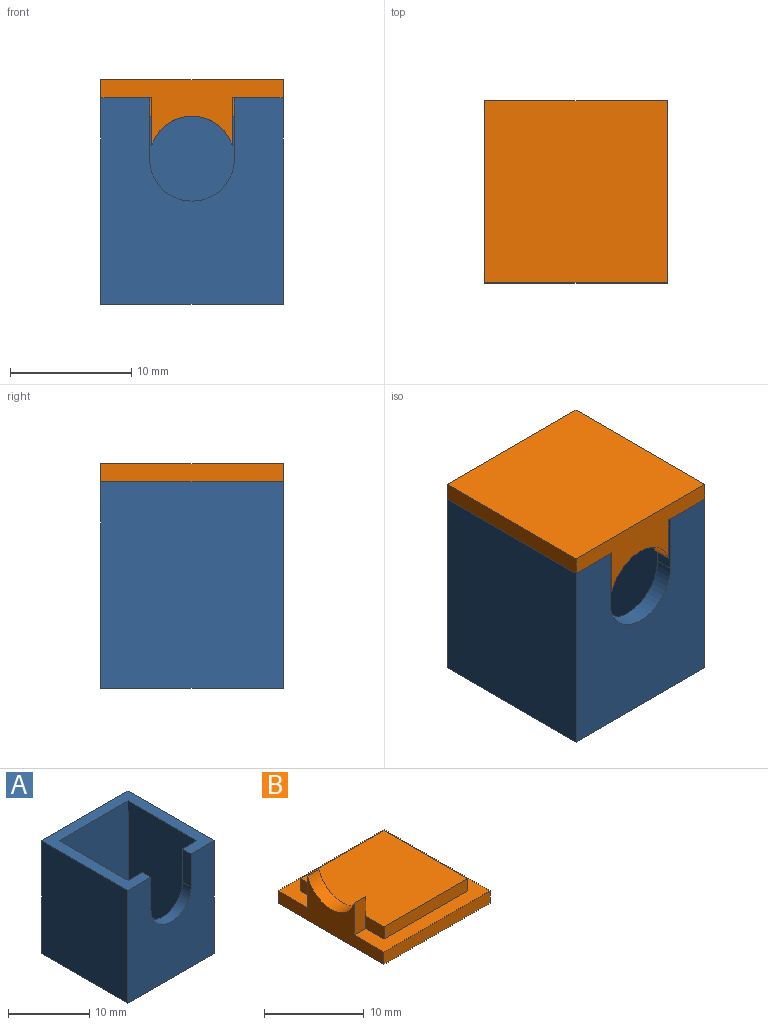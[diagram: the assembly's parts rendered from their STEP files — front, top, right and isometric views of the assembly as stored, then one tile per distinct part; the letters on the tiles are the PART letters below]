
ASSEMBLY  parts=2 mates=1
PART A: 18 faces, bbox 15x15x17 mm
  f0: plane 17x15mm, normal (0,-1,0), area 200.8mm2, adj f1,f3,f8,f9,f15,f16,f17
  f1: plane 15x15mm, normal (0,0,1), area 70.5mm2, adj f0,f2,f3,f4,f5,f6,f7,f8
  f2: plane 17x15mm, normal (0,1,0), area 255mm2, adj f1,f3,f8,f9
  f3: plane 17x15mm, normal (-1,0,0), area 255mm2, adj f0,f1,f2,f9
  f4: plane 15.5x12mm, normal (1,0,0), area 186mm2, adj f1,f5,f7,f14
  f5: plane 15.5x12mm, normal (0,-1,0), area 186mm2, adj f1,f4,f6,f14
  f6: plane 15.5x12mm, normal (-1,0,0), area 186mm2, adj f1,f5,f7,f14
  f7: plane 15.5x12mm, normal (0,1,0), area 131.8mm2, adj f1,f4,f6,f14,f15,f16,f17
  f8: plane 17x15mm, normal (1,0,0), area 255mm2, adj f0,f1,f2,f9
  f9: plane 15x15mm, normal (0,0,-1), area 219mm2, adj f0,f2,f3,f8,f10,f11,f12,f13
  f10: plane 2x1.5mm, normal (-1,0,0), area 3mm2, adj f9,f11,f13,f14
  f11: plane 3x1.5mm, normal (0,1,0), area 4.5mm2, adj f9,f10,f12,f14
  f12: plane 2x1.5mm, normal (1,0,0), area 3mm2, adj f9,f11,f13,f14
  f13: plane 3x1.5mm, normal (0,-1,0), area 4.5mm2, adj f9,f10,f12,f14
  f14: plane 12x12mm, normal (0,0,1), area 138mm2, adj f4,f5,f6,f7,f10,f11,f12,f13
  f15: cylinder r=3.5mm len=7mm, axis (0,-1,0), area 16.5mm2, adj f0,f7,f16,f17
  f16: plane 5x1.5mm, normal (-1,0,0), area 7.5mm2, adj f0,f1,f7,f15
  f17: plane 5x1.5mm, normal (1,0,0), area 7.5mm2, adj f0,f1,f7,f15
PART B: 17 faces, bbox 15x15x5.4 mm
  f0: plane 3.91x1.63mm, normal (0,1,0), area 6.3mm2, adj f2,f4,f14,f15,f16
  f1: plane 3.91x1.63mm, normal (0,-1,0), area 6.3mm2, adj f2,f3,f5,f14,f16
  f2: plane 15x5.41mm, normal (-1,0,0), area 36.8mm2, adj f0,f1,f10,f11,f13,f14,f16
  f3: plane 3.33x2.41mm, normal (1,0,0), area 2.1mm2, adj f1,f9,f16
  f4: plane 2.55x1.5mm, normal (-1,0,0), area 3.8mm2, adj f0,f8,f9,f14
  f5: plane 2.55x1.5mm, normal (-1,0,0), area 3.8mm2, adj f1,f6,f9,f14
  f6: plane 11.75x1.5mm, normal (0,-1,0), area 17.6mm2, adj f5,f7,f9,f14
  f7: plane 11.75x1.5mm, normal (1,0,0), area 17.6mm2, adj f6,f8,f9,f14
  f8: plane 11.75x1.5mm, normal (0,1,0), area 17.6mm2, adj f4,f7,f9,f14
  f9: plane 11.75x11.75mm, normal (0,0,1), area 138.1mm2, adj f3,f4,f5,f6,f7,f8,f15
  f10: plane 15x15mm, normal (0,0,-1), area 225mm2, adj f2,f11,f12,f13
  f11: plane 15x1.5mm, normal (0,-1,0), area 22.5mm2, adj f2,f10,f12,f14
  f12: plane 15x1.5mm, normal (1,0,0), area 22.5mm2, adj f10,f11,f13,f14
  f13: plane 15x1.5mm, normal (0,1,0), area 22.5mm2, adj f2,f10,f12,f14
  f14: plane 15x15mm, normal (0,0,1), area 76.1mm2, adj f0,f1,f2,f4,f5,f6,f7,f8
  f15: plane 3.33x2.41mm, normal (1,0,0), area 2.1mm2, adj f0,f9,f16
  f16: cylinder r=3.5mm len=6.65mm, axis (-1,0,0), area 14.3mm2, adj f0,f1,f2,f3,f15
PLACE A t=(-4.7,1.66,-2.6)mm
PLACE B rot(axis=(0.71,0.71,0),180deg) t=(-4.7,1.66,15.9)mm
MATE fastened B.f14 <-> A.f1  axis (0,0,-1) through (2.8,-5.84,14.4)mm
